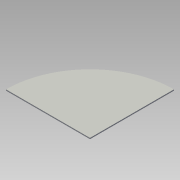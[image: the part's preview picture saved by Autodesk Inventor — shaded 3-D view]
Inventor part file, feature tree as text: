
AUTODESK INVENTOR PART (.ipt)
format: ipt  version: 2015 SP1 (Build 190203100, 203)  size: 79,360 bytes
history: native  units: mm
features: extrude x1, sketch x1
ambient origin geometry x8: Origin, YZ Plane, XZ Plane, XY Plane, X Axis, Y Axis, Z Axis, Center Point
bodies: Solid1 (feature_tree)
feature tree (2):
  extrude  "Extrusion1"  TaperAngle=90.0deg  [1 undecoded]
  sketch  "Sketch1"  dims[d0=300.0mm d1=90.0deg d2=4.0mm d3=0.0mm]
note: 1 required parameter value undecoded (feature->parameter linkage not recoverable at this tier; creation-order binding heuristic only, values carry confidence <= 0.55)
